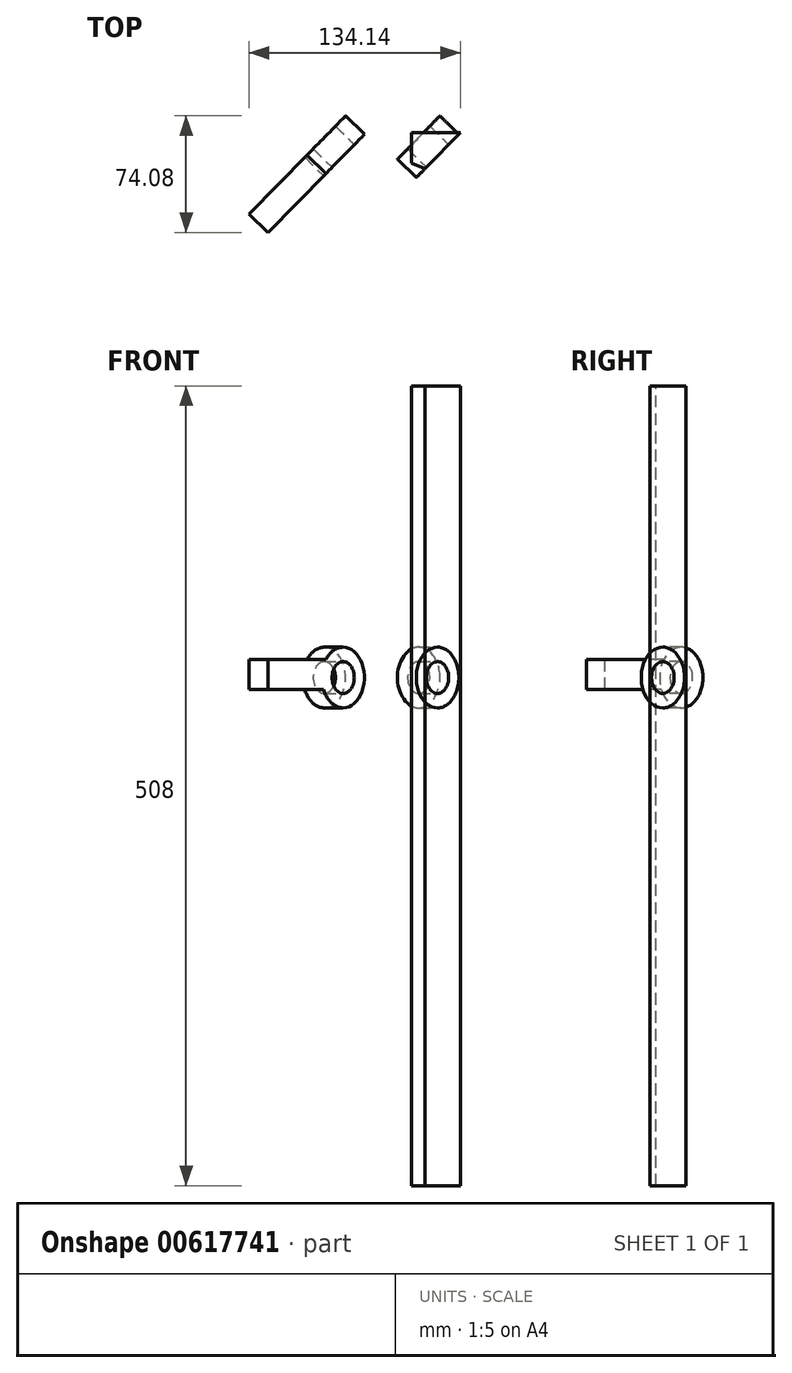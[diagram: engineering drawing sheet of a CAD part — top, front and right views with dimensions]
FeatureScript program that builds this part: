
annotation { "Feature Type Name" : "Feature", "Feature Type Description" : "" }
export const myFeature = defineFeature(function(context is Context, id is Id, definition is map)
    precondition{}
    {
        {
            var Q0;
            Q0=qCreatedBy(makeId("Top.planeOp"),FACE);
            var sketch = newSketch(context, id + "F0", { "sketchPlane" : qUnion([Q0])});
            skLineSegment(sketch, "E0", {"start": v(0, 0) * mm, "end": v(0, 31.76) * mm});
            skLineSegment(sketch, "E1", {"start": v(0, 31.76) * mm, "end": v(31.19, 31.76) * mm});
            skLineSegment(sketch, "E2", {"start": v(31.19, 31.76) * mm, "end": v(0, 0) * mm});
            skSolve(sketch);
        }
        {
            var Q0;
            Q0 = qSketchRegion(id + "F0", true);
            extrude(context, id + "F1", {"entities" : qUnion([Q0]), "depth" : 508 * mm, "offsetDistance" : 25.4 * mm});
        }
        {
            var Q0;
            Q0=makeQuery(id+"F1.opExtrude","SWEPT_FACE",FACE,{"disambiguationData":[OSD([sQuery(id+"F0.wireOp",EDGE,"E2")])]});
            var sketch = newSketch(context, id + "F2", { "sketchPlane" : qUnion([Q0])});
            skCircle(sketch, "E3", {"center": v(23.78, 322.8) * mm, "radius": 19.28 * mm});
            skCircle(sketch, "E4", {"center": v(23.78, 322.8) * mm, "radius": 10.08 * mm});
            skSolve(sketch);
        }
        {
            var Q0;
            Q0 = qSketchRegion(id + "F2", true);
            extrude(context, id + "F3", {"entities" : qUnion([Q0]), "oppositeDirection" : true, "depth" : 16.76 * mm, "offsetDistance" : 25.4 * mm});
        }
        {
            var Q0;
            Q0=makeQuery(id+"F3.opExtrude","SWEPT_BODY",BODY,{"disambiguationData":[OSD([sQuery(id+"F2.wireOp",EDGE,"E3"),sQuery(id+"F2.wireOp",EDGE,"E4")])]});
            transform(context, id + "F4", {"entities" : qUnion([Q0]), "transformType" : TransformType.TRANSLATION_3D, "dx" : -59.94 * mm, "dy" : 0 * mm, "dz" : 0 * mm, "makeCopy" : true});
        }
        {
            var Q0;
            Q0=makeQuery(id+"F4.opPattern","COPY",FACE,{"derivedFrom":makeQuery(id+"F3.opExtrude","CAP_FACE",FACE,{"disambiguationData":[OSD([sQuery(id+"F2.wireOp",EDGE,"E3"),sQuery(id+"F2.wireOp",EDGE,"E4")])],"isStart":true}),"instanceName":"1"});
            var sketch = newSketch(context, id + "F5", { "sketchPlane" : qUnion([Q0])});
            skLineSegment(sketch, "E5.bottom", {"start": v(-86.3, 334.17) * mm, "end": v(-31.77, 334.17) * mm});
            skLineSegment(sketch, "E5.top", {"start": v(-86.3, 315.17) * mm, "end": v(-31.77, 315.17) * mm});
            skLineSegment(sketch, "E5.left", {"start": v(-86.3, 334.17) * mm, "end": v(-86.3, 315.17) * mm});
            skLineSegment(sketch, "E5.right", {"start": v(-31.77, 334.17) * mm, "end": v(-31.77, 315.17) * mm});
            skSolve(sketch);
        }
        {
            var Q0;
            Q0 = qSketchRegion(id + "F5", true);
            var Q1;
            Q1=makeQuery(id+"F4.opPattern","COPY",FACE,{"derivedFrom":makeQuery(id+"F3.opExtrude","CAP_FACE",FACE,{"disambiguationData":[OSD([sQuery(id+"F2.wireOp",EDGE,"E3"),sQuery(id+"F2.wireOp",EDGE,"E4")])],"isStart":false}),"instanceName":"1"});
            extrude(context, id + "F6", {"entities" : qUnion([Q0]), "operationType" : NewBodyOperationType.ADD, "endBound" : BoundingType.UP_TO_SURFACE, "oppositeDirection" : true, "depth" : 25.4 * mm, "endBoundEntityFace" : qUnion([Q1]), "offsetDistance" : 25.4 * mm});
        }
        {
            var Q0;
            Q0=makeQuery(id+"F1.opExtrude","SWEPT_EDGE",EDGE,{"disambiguationData":[OSD([sQuery(id+"F0.wireOp",EDGE,"E0"),sQuery(id+"F0.wireOp",EDGE,"E2")])]});
            chamfer(context, id + "F7", {"entities" : qUnion([Q0]), "width" : 5.08 * mm, "tangentPropagation" : true});
        }
    });
